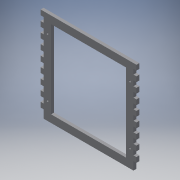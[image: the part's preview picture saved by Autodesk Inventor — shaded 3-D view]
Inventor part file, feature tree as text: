
AUTODESK INVENTOR PART (.ipt)
format: ipt  version: 2019 (Build 230136000, 136)  size: 294,400 bytes
history: native  units: mm
features: reference x20, other x5, extrude x3, sketch x3, projected_geometry x2
ambient origin geometry x8: Origin, YZ Plane, XZ Plane, XY Plane, X Axis, Y Axis, Z Axis, Center Point
bodies: Body1 (feature_tree)
feature tree (33):
  other  "Твердое тело1"
  extrude  "Выдавливание1"  Depth=6.0mm TaperAngle=0.0deg
  extrude  "Выдавливание2"  Depth=15.0mm
  extrude  "Выдавливание3"  Depth=15.0mm
  sketch  "Эскиз1"
  reference  "Ссылка1"
  reference  "Ссылка2"
  reference  "Ссылка3"
  reference  "Ссылка4"
  reference  "Ссылка5"
  reference  "Ссылка6"
  reference  "Ссылка7"
  reference  "Ссылка8"
  reference  "Ссылка9"
  reference  "Ссылка10"
  reference  "Ссылка11"
  reference  "Ссылка12"
  reference  "Ссылка13"
  reference  "Ссылка14"
  reference  "Ссылка15"
  reference  "Ссылка16"
  reference  "Ссылка17"
  reference  "Ссылка18"
  reference  "Ссылка19"
  reference  "Ссылка20"
  sketch  "Эскиз2"
  projected_geometry  "Спроецированная петля1"
  sketch  "Эскиз3"
  projected_geometry  "Спроецированная петля2"
  other  "<userpath>\Desktop\Новая папка (7)\Сборка2.iam"
  other  "Сборка2.iam"
  other  "боковина:1"
  other  "боковина:2"
